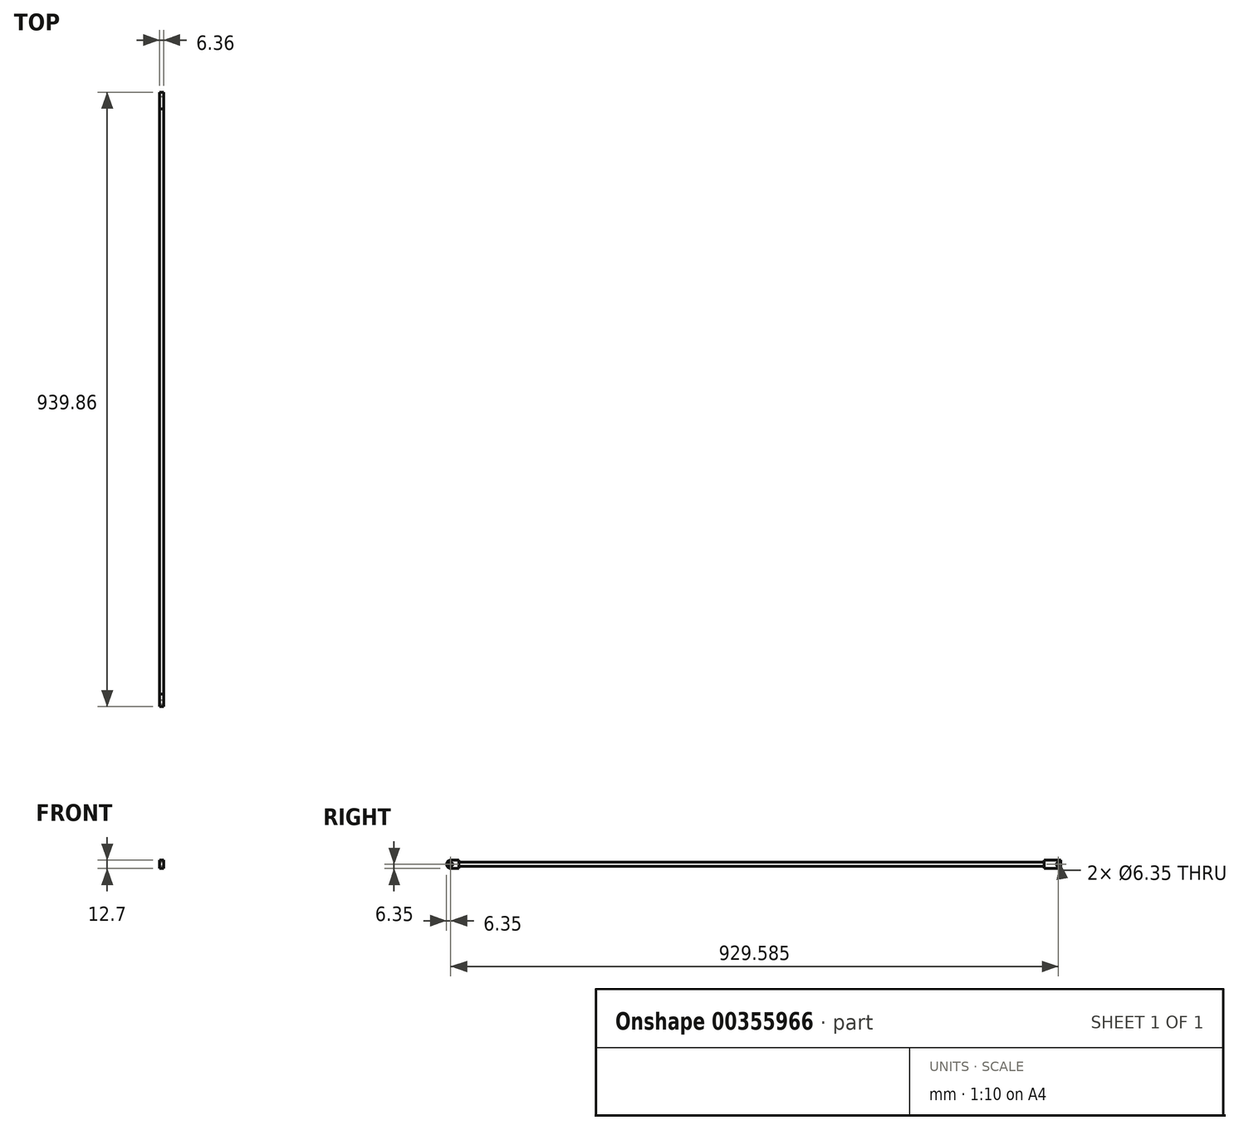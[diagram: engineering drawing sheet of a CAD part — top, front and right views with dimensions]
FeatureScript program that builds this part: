
annotation { "Feature Type Name" : "Feature", "Feature Type Description" : "" }
export const myFeature = defineFeature(function(context is Context, id is Id, definition is map)
    precondition{}
    {
        {
            var Q0;
            Q0=qCreatedBy(makeId("Front.planeOp"),FACE);
            var sketch = newSketch(context, id + "F0", { "sketchPlane" : qUnion([Q0])});
            skCircle(sketch, "E0", {"center": v(0, 0) * mm, "radius": 3.18 * mm});
            skSolve(sketch);
        }
        {
            var Q0;
            Q0=qCreatedBy(makeId("Right.planeOp"),FACE);
            var sketch = newSketch(context, id + "F1", { "sketchPlane" : qUnion([Q0])});
            skLineSegment(sketch, "E1.bottom", {"start": v(6.35, -6.35) * mm, "end": v(-6.35, -6.35) * mm});
            skLineSegment(sketch, "E1.top", {"start": v(6.35, 6.35) * mm, "end": v(-6.35, 6.35) * mm});
            skLineSegment(sketch, "E1.left", {"start": v(6.35, -6.35) * mm, "end": v(6.35, 6.35) * mm});
            skPoint(sketch, "E1.middle", {"position": v(0, 0) * mm});
            skCircle(sketch, "E2", {"center": v(-6.35, 0) * mm, "radius": 6.35 * mm});
            skCircle(sketch, "E3", {"center": v(-6.35, 0) * mm, "radius": 3.18 * mm});
            skSolve(sketch);
        }
        {
            var Q0;
            Q0=makeQuery(id+"F1.imprint","IMPRINT",FACE,{"disambiguationData":[TD([[makeQuery(id+"F1.imprint","IMPRINT",EDGE,{"derivedFrom":sQuery(id+"F1.wireOp",EDGE,"E3")}),-1.0]])]});
            extrude(context, id + "F2", {"entities" : qUnion([Q0]), "endBound" : BoundingType.SYMMETRIC, "depth" : 6.35 * mm});
        }
        {
            var Q0;
            {var subQ0=sQuery(id+"F1.wireOp",EDGE,"E1.bottom");Q0=makeQuery(id+"F1.imprint","IMPRINT",FACE,{"disambiguationData":[TD([[makeQuery(id+"F1.imprint","IMPRINT",EDGE,{"derivedFrom":subQ0}),-1.0]])]});}
            extrude(context, id + "F3", {"entities" : qUnion([Q0]), "operationType" : NewBodyOperationType.ADD, "endBound" : BoundingType.SYMMETRIC, "depth" : 6.35 * mm});
        }
        {
            var Q0;
            Q0=qSketchRegion(id+"F0",true);
            var Q1;
            Q1=sQuery(id+"F0.wireOp",EDGE,"E0");
            extrude(context, id + "F4", {"entities" : qUnion([Q0]), "operationType" : NewBodyOperationType.ADD, "surfaceEntities" : qUnion([Q1]), "oppositeDirection" : true, "depth" : 914.4 * mm});
        }
        {
            var Q0;
            Q0=qCreatedBy(makeId("Right.planeOp"),FACE);
            var sketch = newSketch(context, id + "F5", { "sketchPlane" : qUnion([Q0])});
            skLineSegment(sketch, "E4.bottom", {"start": v(927.16, -6.35) * mm, "end": v(901.76, -6.35) * mm});
            skLineSegment(sketch, "E4.top", {"start": v(927.16, 6.35) * mm, "end": v(901.76, 6.35) * mm});
            skLineSegment(sketch, "E4.left", {"start": v(927.16, -6.35) * mm, "end": v(927.16, 6.35) * mm});
            skLineSegment(sketch, "E4.right", {"start": v(901.76, -6.35) * mm, "end": v(901.76, 6.35) * mm});
            skPoint(sketch, "E4.middle", {"position": v(914.46, 0) * mm});
            skCircle(sketch, "E5", {"center": v(923.23, 0) * mm, "radius": 3.18 * mm});
            skPoint(sketch, "E5.centerSnap0", {"position": v(927.16, 0) * mm});
            skSolve(sketch);
        }
        {
            var Q0;
            Q0=makeQuery(id+"F5.imprint","IMPRINT",FACE,{"disambiguationData":[TD([[makeQuery(id+"F5.imprint","IMPRINT",EDGE,{"derivedFrom":sQuery(id+"F5.wireOp",EDGE,"E4.bottom")}),-1.0]])]});
            extrude(context, id + "F6", {"entities" : qUnion([Q0]), "operationType" : NewBodyOperationType.ADD, "endBound" : BoundingType.SYMMETRIC, "depth" : 6.35 * mm});
        }
    });
